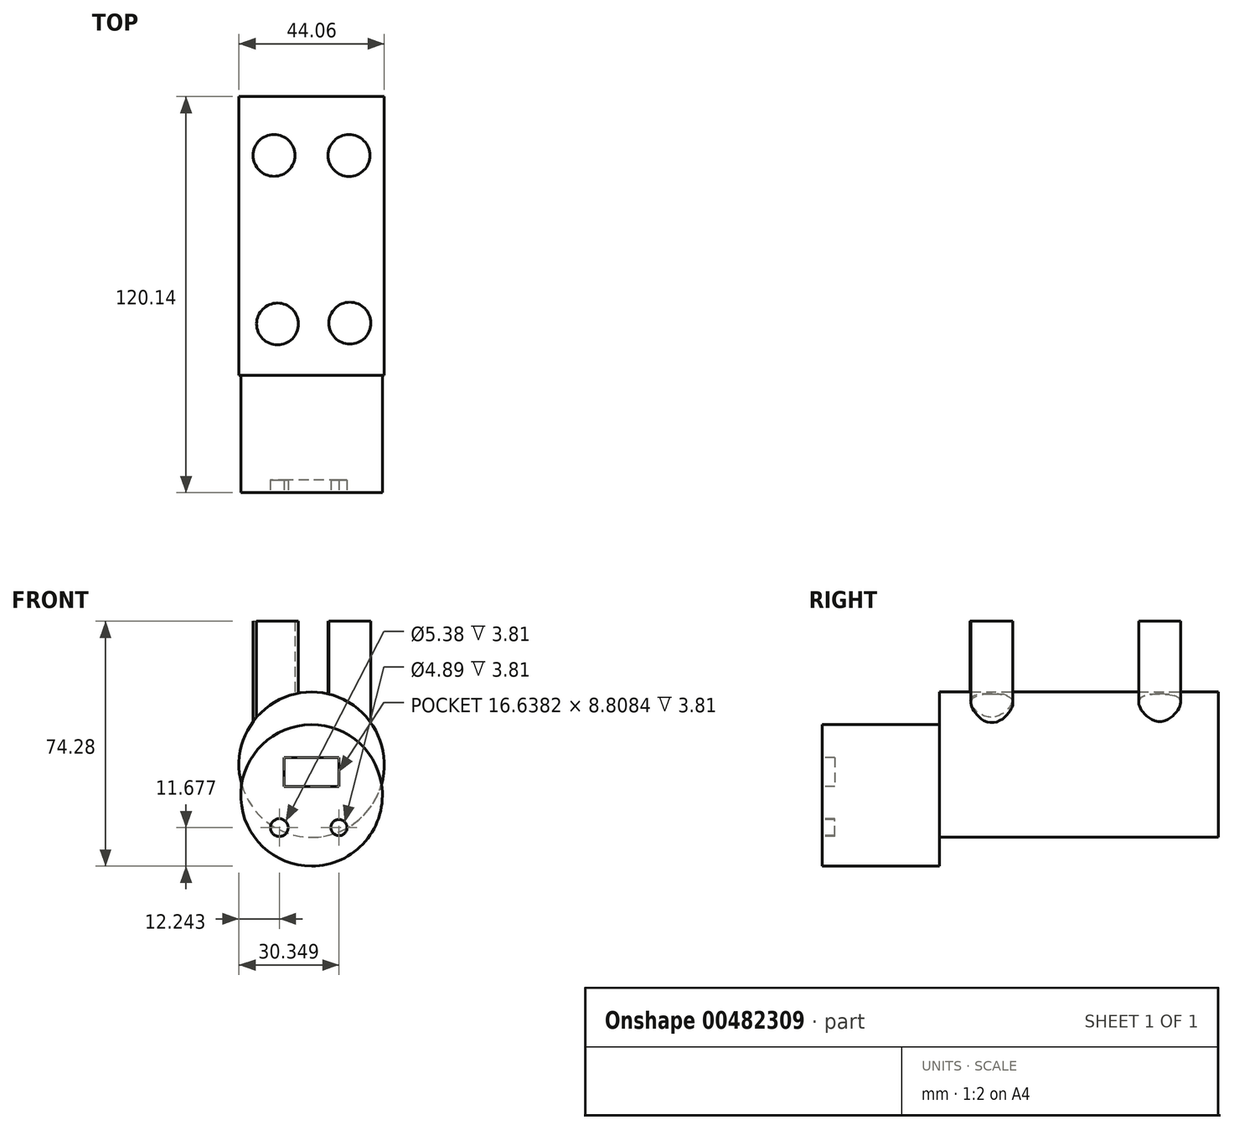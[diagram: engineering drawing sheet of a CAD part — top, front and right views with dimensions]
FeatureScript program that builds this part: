
annotation { "Feature Type Name" : "Feature", "Feature Type Description" : "" }
export const myFeature = defineFeature(function(context is Context, id is Id, definition is map)
    precondition{}
    {
        {
            var Q0;
            Q0=qCreatedBy(makeId("Front.planeOp"),FACE);
            var sketch = newSketch(context, id + "F0", { "sketchPlane" : qUnion([Q0])});
            skCircle(sketch, "E0", {"center": v(0, 2.2) * mm, "radius": 22.03 * mm});
            skSolve(sketch);
        }
        {
            var Q0;
            Q0 = qSketchRegion(id + "F0", true);
            extrude(context, id + "F1", {"entities" : qUnion([Q0]), "depth" : 84.58 * mm});
        }
        {
            var Q0;
            Q0=qCreatedBy(makeId("Top.planeOp"),FACE);
            var sketch = newSketch(context, id + "F2", { "sketchPlane" : qUnion([Q0])});
            skCircle(sketch, "E1", {"center": v(-11.4, -17.84) * mm, "radius": 6.35 * mm});
            skCircle(sketch, "E2", {"center": v(11.36, -17.87) * mm, "radius": 6.35 * mm});
            skCircle(sketch, "E3", {"center": v(-10.33, -68.98) * mm, "radius": 6.35 * mm});
            skCircle(sketch, "E4", {"center": v(11.62, -68.73) * mm, "radius": 6.35 * mm});
            skSolve(sketch);
        }
        {
            var Q0;
            Q0 = qSketchRegion(id + "F2", true);
            extrude(context, id + "F3", {"entities" : qUnion([Q0]), "operationType" : NewBodyOperationType.ADD, "depth" : 45.72 * mm});
        }
        {
            var Q0;
            Q0=makeQuery(id+"F1.opExtrude","CAP_FACE",FACE,{"disambiguationData":[OSD([sQuery(id+"F0.wireOp",EDGE,"E0")])],"isStart":false});
            var sketch = newSketch(context, id + "F4", { "sketchPlane" : qUnion([Q0])});
            skCircle(sketch, "E5", {"center": v(0, -7.1) * mm, "radius": 21.46 * mm});
            skSolve(sketch);
        }
        {
            var Q0;
            Q0 = qSketchRegion(id + "F4", true);
            extrude(context, id + "F5", {"entities" : qUnion([Q0]), "operationType" : NewBodyOperationType.ADD, "depth" : 35.56 * mm});
        }
        {
            var Q0;
            Q0=makeQuery(id+"F5.opExtrude","CAP_FACE",FACE,{"disambiguationData":[OSD([sQuery(id+"F4.wireOp",EDGE,"E5")])],"isStart":false});
            var sketch = newSketch(context, id + "F6", { "sketchPlane" : qUnion([Q0])});
            skCircle(sketch, "E6", {"center": v(-9.79, -16.88) * mm, "radius": 2.7 * mm});
            skCircle(sketch, "E7", {"center": v(8.32, -16.88) * mm, "radius": 2.45 * mm});
            skLineSegment(sketch, "E8.bottom", {"start": v(8.32, 4.4) * mm, "end": v(-8.32, 4.4) * mm});
            skLineSegment(sketch, "E8.top", {"start": v(8.32, -4.4) * mm, "end": v(-8.32, -4.4) * mm});
            skLineSegment(sketch, "E8.left", {"start": v(8.32, 4.4) * mm, "end": v(8.32, -4.4) * mm});
            skLineSegment(sketch, "E8.right", {"start": v(-8.32, 4.4) * mm, "end": v(-8.32, -4.4) * mm});
            skPoint(sketch, "E8.middle", {"position": v(0, 0) * mm});
            skSolve(sketch);
        }
        {
            var Q0;
            Q0 = qSketchRegion(id + "F6", true);
            extrude(context, id + "F7", {"entities" : qUnion([Q0]), "operationType" : NewBodyOperationType.REMOVE, "oppositeDirection" : true, "depth" : 3.8 * mm});
        }
    });
